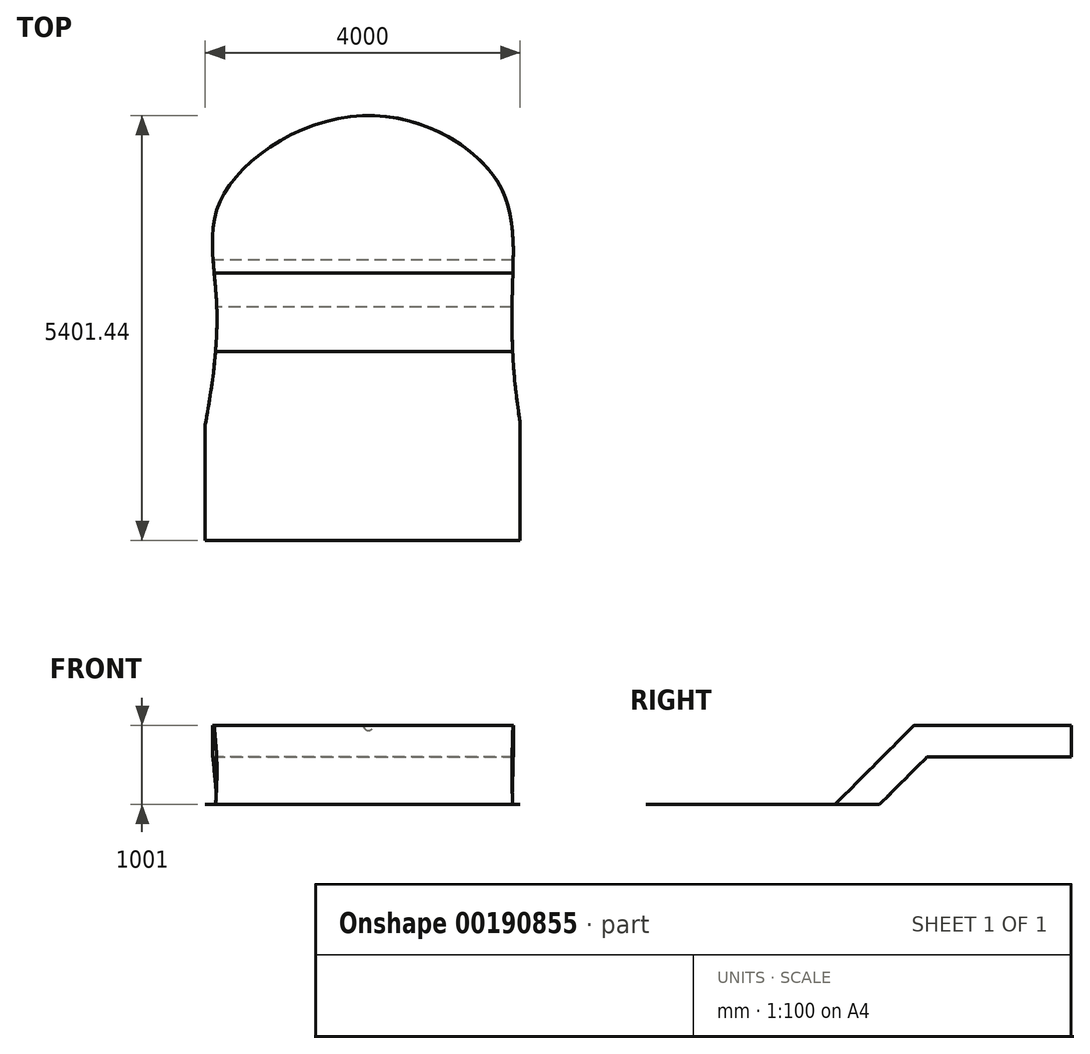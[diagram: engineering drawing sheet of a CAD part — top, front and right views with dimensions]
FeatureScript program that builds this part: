
annotation { "Feature Type Name" : "Feature", "Feature Type Description" : "" }
export const myFeature = defineFeature(function(context is Context, id is Id, definition is map)
    precondition{}
    {
        {
            var Q0;
            Q0=qCreatedBy(makeId("Right.planeOp"),FACE);
            var sketch = newSketch(context, id + "F0", { "sketchPlane" : qUnion([Q0])});
            skLineSegment(sketch, "E0", {"start": v(-2400, 0) * mm, "end": v(0, 0) * mm});
            skLineSegment(sketch, "E1", {"start": v(0, 0) * mm, "end": v(1000, 1000) * mm});
            skLineSegment(sketch, "E2", {"start": v(1000, 1000) * mm, "end": v(3000, 1000) * mm});
            skLineSegment(sketch, "E3", {"start": v(-2400, 0) * mm, "end": v(-2400, -1) * mm});
            skLineSegment(sketch, "E4", {"start": v(-2400, -1) * mm, "end": v(564.69, -1) * mm});
            skLineSegment(sketch, "E5", {"start": v(564.69, -1) * mm, "end": v(1165.69, 600) * mm});
            skLineSegment(sketch, "E6", {"start": v(1165.69, 600) * mm, "end": v(3009.14, 600) * mm});
            skLineSegment(sketch, "E7", {"start": v(3009.14, 600) * mm, "end": v(3000, 1000) * mm});
            skSolve(sketch);
        }
        {
            var Q0;
            Q0 = qSketchRegion(id + "F0", true);
            var Q1;
            Q1=sQuery(id+"F0.wireOp",EDGE,"E0");
            extrude(context, id + "F1", {"entities" : qUnion([Q0]), "surfaceEntities" : qUnion([Q1]), "endBound" : BoundingType.SYMMETRIC, "depth" : 4000 * mm});
        }
        {
            var Q0;
            Q0=qCreatedBy(makeId("Top.planeOp"),FACE);
            var sketch = newSketch(context, id + "F2", { "sketchPlane" : qUnion([Q0])});
            skFitSpline(sketch, "E8", {"points": [v(-2150.77, -1639.49) * mm, v(-1855.47, 594.95) * mm, v(-1786.56, 1963.17) * mm, v(0, 3000) * mm, v(1717.66, 2150.2) * mm, v(1894.84, 476.83) * mm, v(2239.36, -1482) * mm, v(2633.09, -1413.09) * mm], "startDerivative": vector(3217.43, 13972.9) * mm, "endDerivative": vector(5847.16, 3240.37) * mm});
            skLineSegment(sketch, "E9", {"start": v(-2150.77, -1639.49) * mm, "end": v(-2150.77, 3114.84) * mm});
            skLineSegment(sketch, "E10", {"start": v(-2150.77, 3114.84) * mm, "end": v(2485.44, 3114.84) * mm});
            skLineSegment(sketch, "E11", {"start": v(2485.44, 3114.84) * mm, "end": v(2633.09, -1413.09) * mm});
            skSolve(sketch);
        }
        {
            var Q0;
            Q0 = qSketchRegion(id + "F2", true);
            extrude(context, id + "F3", {"entities" : qUnion([Q0]), "operationType" : NewBodyOperationType.REMOVE, "endBound" : BoundingType.THROUGH_ALL, "depth" : 25 * mm, "hasSecondDirection" : true, "secondDirectionOppositeDirection" : true, "secondDirectionDepth" : 25 * mm});
        }
    });
